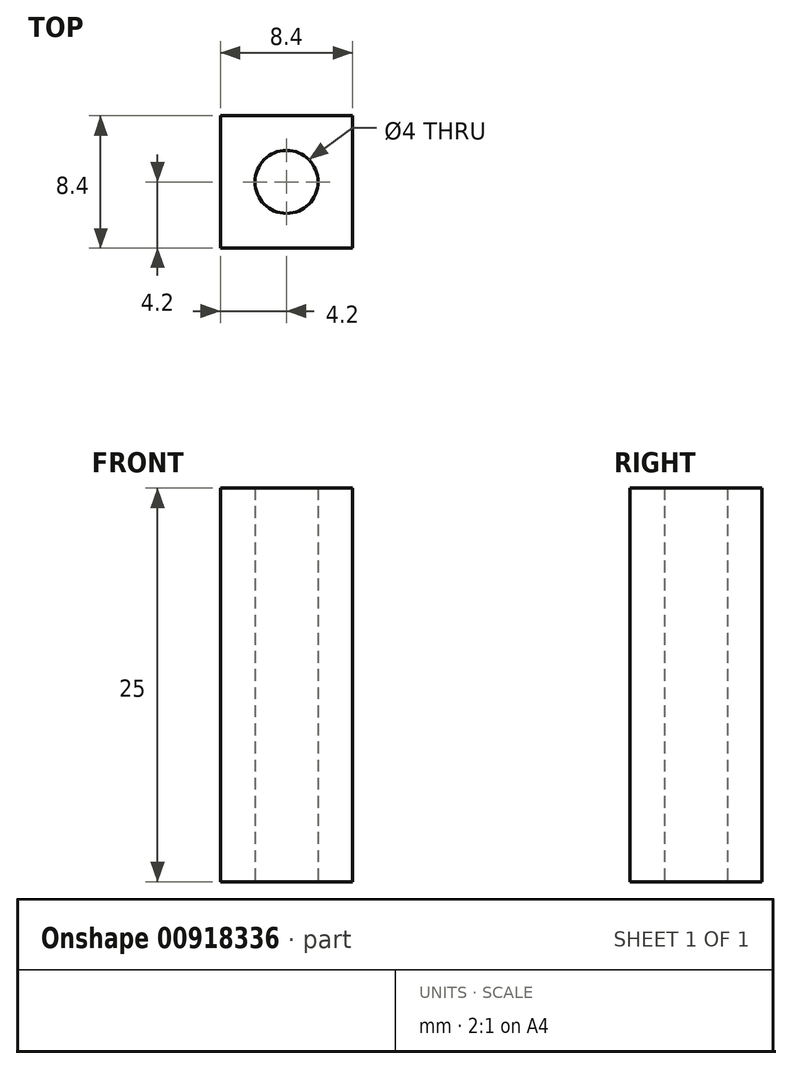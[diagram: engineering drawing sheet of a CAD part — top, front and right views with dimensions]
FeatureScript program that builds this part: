
annotation { "Feature Type Name" : "Feature", "Feature Type Description" : "" }
export const myFeature = defineFeature(function(context is Context, id is Id, definition is map)
    precondition{}
    {
        {
            var Q0;
            Q0=qCreatedBy(makeId("Top.planeOp"),FACE);
            var sketch = newSketch(context, id + "F0", { "sketchPlane" : qUnion([Q0])});
            skLineSegment(sketch, "E0.bottom", {"start": v(-4.2, 4.2) * mm, "end": v(4.2, 4.2) * mm});
            skLineSegment(sketch, "E0.top", {"start": v(-4.2, -4.2) * mm, "end": v(4.2, -4.2) * mm});
            skLineSegment(sketch, "E0.left", {"start": v(-4.2, 4.2) * mm, "end": v(-4.2, -4.2) * mm});
            skLineSegment(sketch, "E0.right", {"start": v(4.2, 4.2) * mm, "end": v(4.2, -4.2) * mm});
            skPoint(sketch, "E0.middle", {"position": v(0, 0) * mm});
            skCircle(sketch, "E1", {"center": v(0, 0) * mm, "radius": 2 * mm});
            skSolve(sketch);
        }
        {
            var Q0;
            Q0=makeQuery(id+"F0.imprint","IMPRINT",FACE,{"disambiguationData":[TD([[makeQuery(id+"F0.imprint","IMPRINT",EDGE,{"derivedFrom":sQuery(id+"F0.wireOp",EDGE,"E0.bottom")}),-1.0]])]});
            extrude(context, id + "F1", {"entities" : qUnion([Q0]), "depth" : 25 * mm, "offsetDistance" : 25 * mm});
        }
    });
